# Revit family: BE_77277_de_DE
name_source: partatom
category: Leuchten
revit_build: Autodesk Revit 2015 (Build: 20151008_0715(x64)
units: mm (PartAtom-declared; Revit-internal decimal feet)

## types (2) — shared parameters
AC/DC = AC/DC
Aktualisierung = 2015-11-11T04:07:44
BEGA_Dummy = Nein
BEGA_IES = Ja
BEGA_Intern = Ja
BEGA_Intern_Konstruktion = Ja
BEGA_Intern_an = Ja
BEGA_Intern_aus = Ja
Befestigungsbohrung = Ø 4,5 mm
Beschreibung = Gartenleuchte
Beschreibung_Sonderanfertigung = Hier können Sie Informationen zur Sonderanfertigung eintragen.
CE_Konformität = ja
Datei für fotometrisches Netz = BE_77277.IES
Energieeffizienzklasse = LED A++ - A
Farbfilter = 16777215
Farbtemperatur = 3000 K
Farbtemperaturverschiebung bei Dämpfen der Lampe = <Keine Auswahl>
Farbwiedergabeindex = Ra > 80
Frequenz = 0/50-60 Hz
Gewicht = 1.1 kg
Hersteller = BEGA
LED_Modulbezeichnung = LED-0490/830
Lampe = LED 6.3 W
Lampenlichtstrom = 735 lm
Lastklassifizierung = Beleuchtung
Lebensdauerkriterien = L70 = 50.000 h
Leuchtenlichtstrom = 190 lm
Logo = BEGA_Logo.png
Material_02 = BEGA_Oberfläche_Silber_matt
Material_06 = BEGA_Oberfläche_Edelstahl_gebürstet
Material_08 = BEGA_Oberfläche_Stahl_verzinkt
Material_10 = BEGA_Glas_matt
Material_15 = BEGA_Leuchtmedium_matt
Material_19 = BEGA_Dummy_matt
Neigungswinkel = 0.00°
Produktdatenblatt = http://www.bega.de
Scheinlast = 0 VA
Schutzart = IP 65
Schutzklasse = I
Sonderanfertigung = Nein
Spannung = 0 V
Typenbild = 77277.png
URL = http://www.bega.de
Umgebungstemperatur = 25 °C
zero-valued in all types: Vorgabe-Ansicht

## per-type parameters (varying)
| type | Bestellnummer | M_A | M_G | Modell |
| BEGA_77277_Grafit_K3 | 77277 | Nein | Ja | 77277 |
| BEGA_77277_Silber_K3 | 77277A | Ja | Nein | 77277A |
